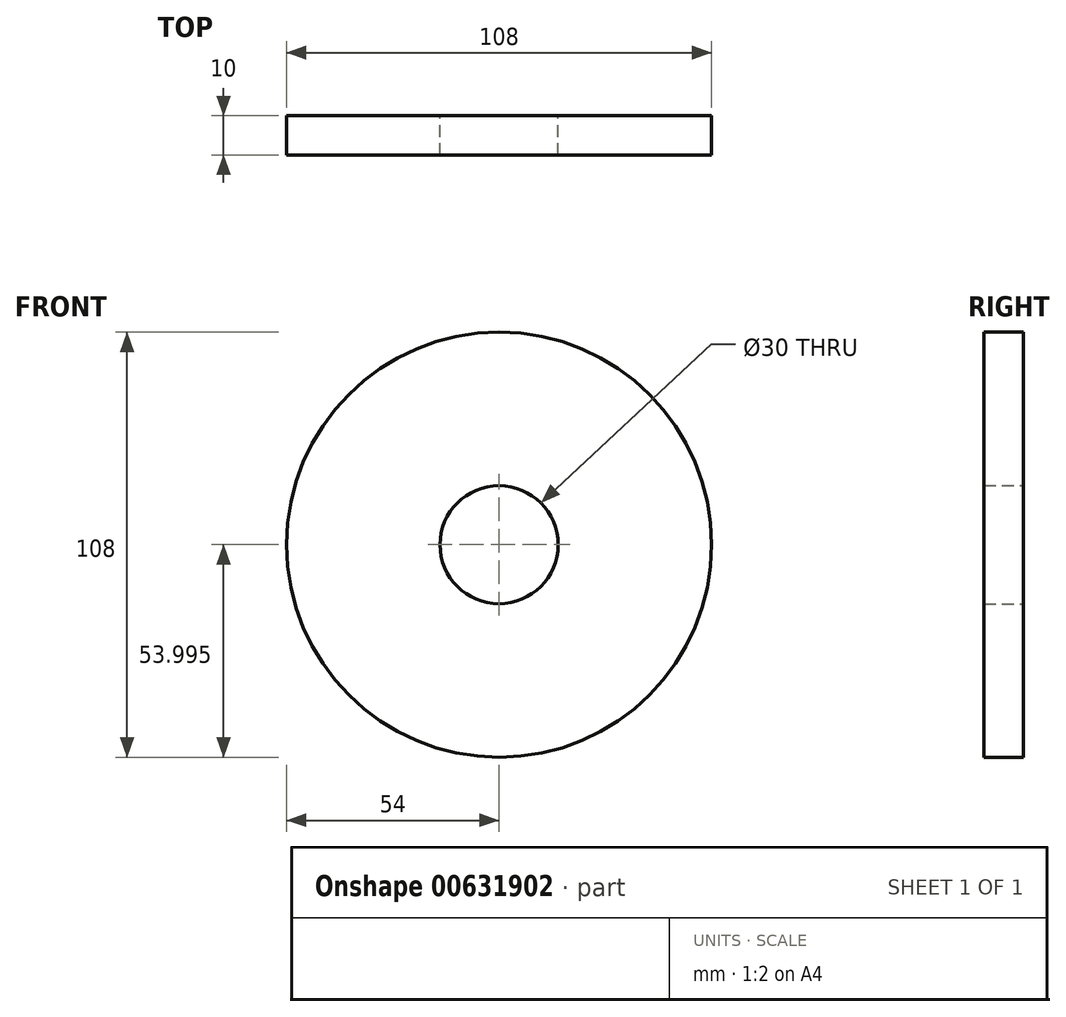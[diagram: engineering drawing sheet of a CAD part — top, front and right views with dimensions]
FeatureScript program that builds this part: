
annotation { "Feature Type Name" : "Feature", "Feature Type Description" : "" }
export const myFeature = defineFeature(function(context is Context, id is Id, definition is map)
    precondition{}
    {
        {
            var Q0;
            Q0=qCreatedBy(makeId("Front.planeOp"),FACE);
            var sketch = newSketch(context, id + "F0", { "sketchPlane" : qUnion([Q0])});
            skCircle(sketch, "E0", {"center": v(-62.85, 41.26) * mm, "radius": 54 * mm});
            skCircle(sketch, "E1", {"center": v(-62.85, 41.26) * mm, "radius": 15 * mm});
            skSolve(sketch);
        }
        {
            var Q0;
            Q0 = qSketchRegion(id + "F0", true);
            extrude(context, id + "F1", {"entities" : qUnion([Q0]), "depth" : 10 * mm, "offsetDistance" : 25 * mm});
        }
    });
